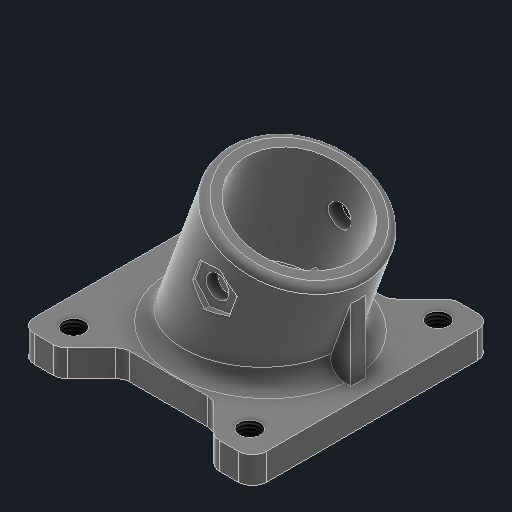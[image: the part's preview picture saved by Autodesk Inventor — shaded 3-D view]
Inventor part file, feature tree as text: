
AUTODESK INVENTOR PART (.ipt)
format: ipt  version: 2025 (Build 290162010, 162A)  size: 502,272 bytes
history: native  units: mm
features: sketch x11, extrude x10, plane x5, fillet x4, thread x4, projected_geometry x2
ambient origin geometry x8: Origin, YZ Plane, XZ Plane, XY Plane, X Axis, Y Axis, Z Axis, Center Point
bodies: Solid1 (feature_tree)
feature tree (36):
  extrude  "Extrusion1"  Depth=26.8mm
  fillet  "Fillet1"  Radius=3.0mm
  thread  "Thread5"  [1 undecoded]
  thread  "Thread6"  [1 undecoded]
  thread  "Thread7"  [1 undecoded]
  thread  "Thread8"  [1 undecoded]
  plane  "Work Plane2"
  sketch  "Sketch8"  dims[d7=34.0mm d8=5.5mm]
  plane  "Work Plane3"
  extrude  "Extrusion6"  Depth=5.5mm
  extrude  "Extrusion8"  Depth=12.375mm
  extrude  "Extrusion9"  Depth=3.8mm TaperAngle=0.0deg
  extrude  "Extrusion10"  Depth=3.8mm TaperAngle=0.0deg
  fillet  "Fillet4"  Radius=3.8mm
  fillet  "Fillet5"  Radius=3.8mm
  fillet  "Fillet6"  Radius=3.8mm
  extrude  "Extrusion11"  Depth=3.490659mm
  extrude  "Extrusion12"  Depth=16.0mm
  plane  "Work Plane4"
  extrude  "Extrusion13"  Depth=26.5mm TaperAngle=0.0deg
  plane  "Work Plane5"
  plane  "Work Plane6"
  extrude  "Extrusion14"  Depth=1.0mm
  extrude  "Extrusion15"  Depth=17.0mm
  sketch  "Sketch1"  dims[d0=25.0mm d1=26.8mm d2=3.0mm d3=3.0mm d4=3.0mm d5=3.0mm d6=33.0mm]
  projected_geometry  "Projected Loop4"
  sketch  "Sketch9"  dims[d9=5.5mm d10=12.375mm]
  projected_geometry  "Projected Loop5"
  sketch  "Sketch11"  dims[d11=45.0deg d12=3.8mm d13=0.0mm]
  sketch  "Sketch12"  dims[d14=2.0mm d49=3.8mm d50=0.0mm d51=3.8mm d52=0.0mm d53=3.8mm d54=0.0mm d55=3.8mm d56=0.0mm]
  sketch  "Sketch13"  dims[d58=13.4088mm d59=3.490659mm]
  sketch  "Sketch14"  dims[d63=11.0075mm d64=16.0mm]
  sketch  "Sketch15"  dims[d65=20.5mm d66=26.5mm d67=0.0mm]
  sketch  "Sketch16"  dims[d72=17.0mm d73=1.0mm]
  sketch  "Sketch17"  dims[d74=1.0mm d75=17.0mm]
  sketch  "Sketch18"  dims[d76=26.5mm d77=0.0mm d78=30.0mm d79=10.0mm d80=0.0mm d81=0.0mm d82=16.0mm d83=15.0mm d84=0.0mm d85=2.0mm d86=2.0mm d87=1.0mm d88=2.0mm d89=1.0mm d90=5.0mm d91=2.0mm d92=5.0mm d93=13.25mm d94=0.0mm d95=16.0mm d96=12.5mm d97=0.0mm d98=6.25mm d99=3.2mm d100=0.0mm d101=0.0mm d102=10.25mm d103=-10.25mm d104=6.25mm d105=3.2mm d106=1.5mm d107=0.0mm d108=6.25mm d109=12.217305mm d110=6.05mm d111=1.0mm d112=0.0mm]
note: 4 required parameter values undecoded (feature->parameter linkage not recoverable at this tier; creation-order binding heuristic only, values carry confidence <= 0.55)
